# Revit family: hansgrohe_Xuniva-S-Above-counter-basin-400-400-wit_(61054XXX)_NEW
name_source: partatom
category: Plumbing Fixtures
revit_build: Autodesk Revit 2018 (Build: 20170223_1515(x64)
units: mm (PartAtom-declared; Revit-internal decimal feet)

## family parameters
Cut with Voids When Loaded = No
Host = Face
OmniClass Number = 23.31.13.00
OmniClass Title = Sinks
Part Type = Normal
Room Calculation Point = No
Round Connector Dimension = Use Diameter
Shared = No

## types (1)
- 450 White
    Connector Description = Water Outlet 46 mm
    Default Elevation = 1219 mm
    Description = Xuniva S Above counter basin 400/400 without tap hole with overflow, SmartClean
    Design country = Germany
    Diameter = 46  [stored 0.150919 ft]
    EAN code = 4059625475294
    Edition number = 1
    IFC Classification = Sanitary Terminal
    Manufacturer = Hansgrohe
    Manufacturer country = Germany
    Manufacturer name = hansgrohe
    Masterformat 2014 Code = 22 41 16.13
    Masterformat 2014 Description = Residential Lavatories
    Material 1 = Hansgrohe - Ceramic - 450 White
    Model = 61054XXX
    OmniClass Code = 23-31 13 00
    OmniClass Description = Sinks
    Product Guid = c6c2ba4c-da67-4f5e-8dce-18b05bd05b21
    Product SKU = 61054XXX
    Product data url = https://bimobject.com
    Product family = Xuniva S
    Product group = Washbasins
    Product name = Xuniva S Above counter basin 400/400 without tap hole with overflow, SmartClean
    QR code = https://bimobject.com
    UNSPSC Code = 301815
    URL = https://www.hansgrohe.com
    Uniclass 2015 Code = Pr_40_20_96
    Uniclass 2015 Name = Wash basins, sinks and troughs
    Uniformat II Code = D2010
    Uniformat II Description = Plumbing Fixtures
    Version = 1
    Weight Net (Kg) = 6

note: [stored X ft] marks values corroborated as IEEE doubles in the binary element streams (Revit-internal decimal feet)

## geometry (parser evidence)
native form markers: Sweep x6
no freeform markers — native parametric forms only
